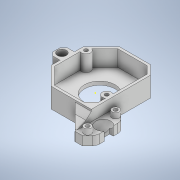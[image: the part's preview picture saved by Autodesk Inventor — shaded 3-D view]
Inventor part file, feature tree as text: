
AUTODESK INVENTOR PART (.ipt)
format: ipt  version: 2020 (Build 240168000, 168)  size: 607,232 bytes
history: native  units: mm
features: sketch x32, extrude x29, projected_geometry x13, chamfer x5, plane x1, revolve x1, fillet x1
ambient origin geometry x8: Origin, YZ Plane, XZ Plane, XY Plane, X Axis, Y Axis, Z Axis, Center Point
bodies: Volumenkörper1 (feature_tree)
feature tree (82):
  extrude  "Extrusion1"  Depth=21.5mm
  extrude  "Extrusion2"  Depth=5.5mm
  extrude  "Extrusion3"  Depth=5.5mm
  extrude  "Extrusion7"  Depth=5.5mm
  extrude  "Extrusion8"  Depth=5.5mm
  extrude  "Extrusion15"  Depth=2.0mm
  extrude  "Extrusion16"  Depth=5.5mm
  plane  "Arbeitsebene1"
  revolve  "Umdrehung1"
  extrude  "Extrusion17"  Depth=5.5mm
  extrude  "Extrusion18"  Depth=5.5mm
  extrude  "Extrusion19"  Depth=5.5mm
  extrude  "Extrusion20"  Depth=2.0mm TaperAngle=0.0deg
  sketch  "Skizze24"  dims[d26=2.0mm]
  extrude  "Extrusion21"  Depth=2.0mm
  sketch  "Skizze26"  dims[d28=4.0mm]
  chamfer  "Fase2"  Distance=5.0mm
  fillet  "Rundung2"  Radius=5.0mm
  extrude  "Extrusion22"  Depth=8.0mm TaperAngle=0.0deg
  extrude  "Extrusion23"  Depth=0.5mm
  extrude  "Extrusion24"  Depth=5.0mm
  extrude  "Extrusion25"  Depth=5.0mm
  extrude  "Extrusion26"  Depth=5.0mm
  extrude  "Extrusion27"  Depth=5.0mm
  extrude  "Extrusion28"  Depth=10.0mm TaperAngle=0.0deg
  extrude  "Extrusion29"  Depth=8.5mm
  extrude  "Extrusion30"  Depth=7.0mm TaperAngle=0.0deg
  extrude  "Extrusion31"  Depth=4.0mm TaperAngle=0.0deg
  extrude  "Extrusion32"  Depth=4.0mm
  extrude  "Extrusion33"  Depth=4.0mm
  extrude  "Extrusion34"  Depth=3.0mm
  extrude  "Extrusion35"  TaperAngle=0.0deg  [1 undecoded]
  extrude  "Extrusion36"  Depth=4.0mm
  chamfer  "Fase3"  Distance=4.0mm
  chamfer  "Fase4"  Distance=3.0mm
  chamfer  "Fase5"  Distance=4.0mm Angle=45.0deg
  extrude  "Extrusion37"  Depth=4.0mm
  extrude  "Extrusion38"  Depth=10.0mm TaperAngle=0.0deg
  chamfer  "Fase6"  Distance=3.6mm
  sketch  "Skizze1"  dims[d0=21.5mm d1=55.0mm]
  sketch  "Skizze3"  dims[d2=5.5mm d3=5.5mm]
  projected_geometry  "Projizierte Kontur1"
  sketch  "Skizze4"  dims[d4=5.5mm d5=5.5mm]
  sketch  "Skizze8"  dims[d6=5.5mm d7=5.5mm]
  sketch  "Skizze9"  dims[d8=5.5mm d9=5.5mm]
  sketch  "Skizze17"  dims[d10=2.0mm d11=2.0mm]
  sketch  "Skizze18"  dims[d12=5.5mm d13=5.5mm]
  projected_geometry  "Projizierte Kontur5"
  sketch  "Skizze19"  dims[d14=5.5mm d15=5.5mm]
  sketch  "Skizze20"  dims[d16=5.5mm d17=5.5mm]
  sketch  "Skizze21"  dims[d18=5.5mm d19=5.5mm]
  sketch  "Skizze22"  dims[d20=10.0mm d21=0.0mm d22=2.0mm d23=0.0mm]
  sketch  "Skizze23"  dims[d24=2.0mm d25=21.0mm]
  sketch  "Skizze25"  dims[d27=18.3mm]
  sketch  "Skizze27"  dims[d29=4.0mm]
  projected_geometry  "Projizierte Kontur6"
  projected_geometry  "Projizierte Kontur7"
  sketch  "Skizze28"  dims[d30=1.1mm]
  sketch  "Skizze29"  dims[d31=1.1mm d32=5.0mm d33=0.0mm d44=5.0mm]
  projected_geometry  "Projizierte Kontur8"
  sketch  "Skizze30"  dims[d45=8.0mm d46=0.0mm d47=12.0mm d48=0.0mm]
  sketch  "Skizze31"  dims[d74=0.5mm d75=0.5mm]
  projected_geometry  "Projizierte Kontur9"
  projected_geometry  "Projizierte Kontur10"
  sketch  "Skizze32"  dims[d80=5.0mm d81=5.0mm]
  sketch  "Skizze33"  dims[d82=5.0mm d83=5.0mm]
  sketch  "Skizze34"  dims[d84=5.0mm d85=5.0mm]
  projected_geometry  "Projizierte Kontur11"
  sketch  "Skizze35"  dims[d86=5.0mm d87=5.0mm]
  projected_geometry  "Projizierte Kontur12"
  sketch  "Skizze36"  dims[d88=10.0mm d89=0.0mm d90=10.0mm d91=0.0mm]
  projected_geometry  "Projizierte Kontur13"
  sketch  "Skizze37"  dims[d92=-6.0mm d93=8.5mm]
  sketch  "Skizze38"  dims[d94=90.0deg d95=7.0mm d96=0.0mm]
  sketch  "Skizze39"  dims[d97=5.0mm d98=4.0mm d99=0.0mm]
  projected_geometry  "Projizierte Kontur14"
  sketch  "Skizze40"  dims[d100=2.0mm d101=0.0mm d102=4.0mm]
  sketch  "Skizze41"  dims[d103=3.0mm d104=4.0mm]
  sketch  "Skizze42"  dims[d105=3.0mm d106=2.1mm]
  projected_geometry  "Projizierte Kontur15"
  sketch  "Skizze43"  dims[d107=2.1mm d108=0.0mm d109=0.0mm d110=4.0mm d111=4.0mm d112=3.0mm d113=0.0mm d114=4.0mm d115=2.0mm d116=45.0deg d117=4.0mm d118=10.0mm d119=0.0mm d120=3.6mm d121=10.0mm d122=5.0mm d123=2.1mm d124=13.0mm d125=11.7mm d126=2.1mm d127=5.0mm d128=9.0mm d129=0.0mm d130=5.0mm d131=0.0mm d132=38.0mm d133=29.6mm d134=10.0mm d135=10.0mm d136=10.0mm d137=10.0mm d138=5.0mm d139=5.0mm d140=5.0mm d141=0.0mm d142=0.0mm d143=0.0mm d144=0.0mm d145=0.0mm d146=17.0mm d147=0.0mm d148=0.0mm d149=1.4mm d150=1.4mm d151=1.4mm d152=1.4mm d153=1.4mm d154=1.4mm d155=1.4mm d156=9.0mm d157=0.0mm d158=9.0mm d159=0.0mm d160=10.0mm d161=0.0mm d162=10.0mm d163=0.0mm d164=2.1mm d165=1.05mm d166=1.05mm d167=9.0mm d168=0.0mm d169=5.0mm d170=10.0mm d171=0.0mm d172=2.0mm d173=0.0mm d174=5.0mm d175=3.0mm d177=4.0mm d178=4.0mm d179=3.0mm d180=5.0mm d181=0.0mm d182=2.0mm d183=2.0mm d184=45.0deg d185=9.0mm d186=2.0mm d187=45.0deg d188=5.0mm d189=2.0mm d190=45.0deg d191=5.0mm d192=0.0mm d193=6.0mm d194=0.0mm d195=3.0mm d196=2.0mm d197=45.0deg]
  projected_geometry  "Projizierte Kontur16"
note: 1 required parameter value undecoded (feature->parameter linkage not recoverable at this tier; creation-order binding heuristic only, values carry confidence <= 0.55)
